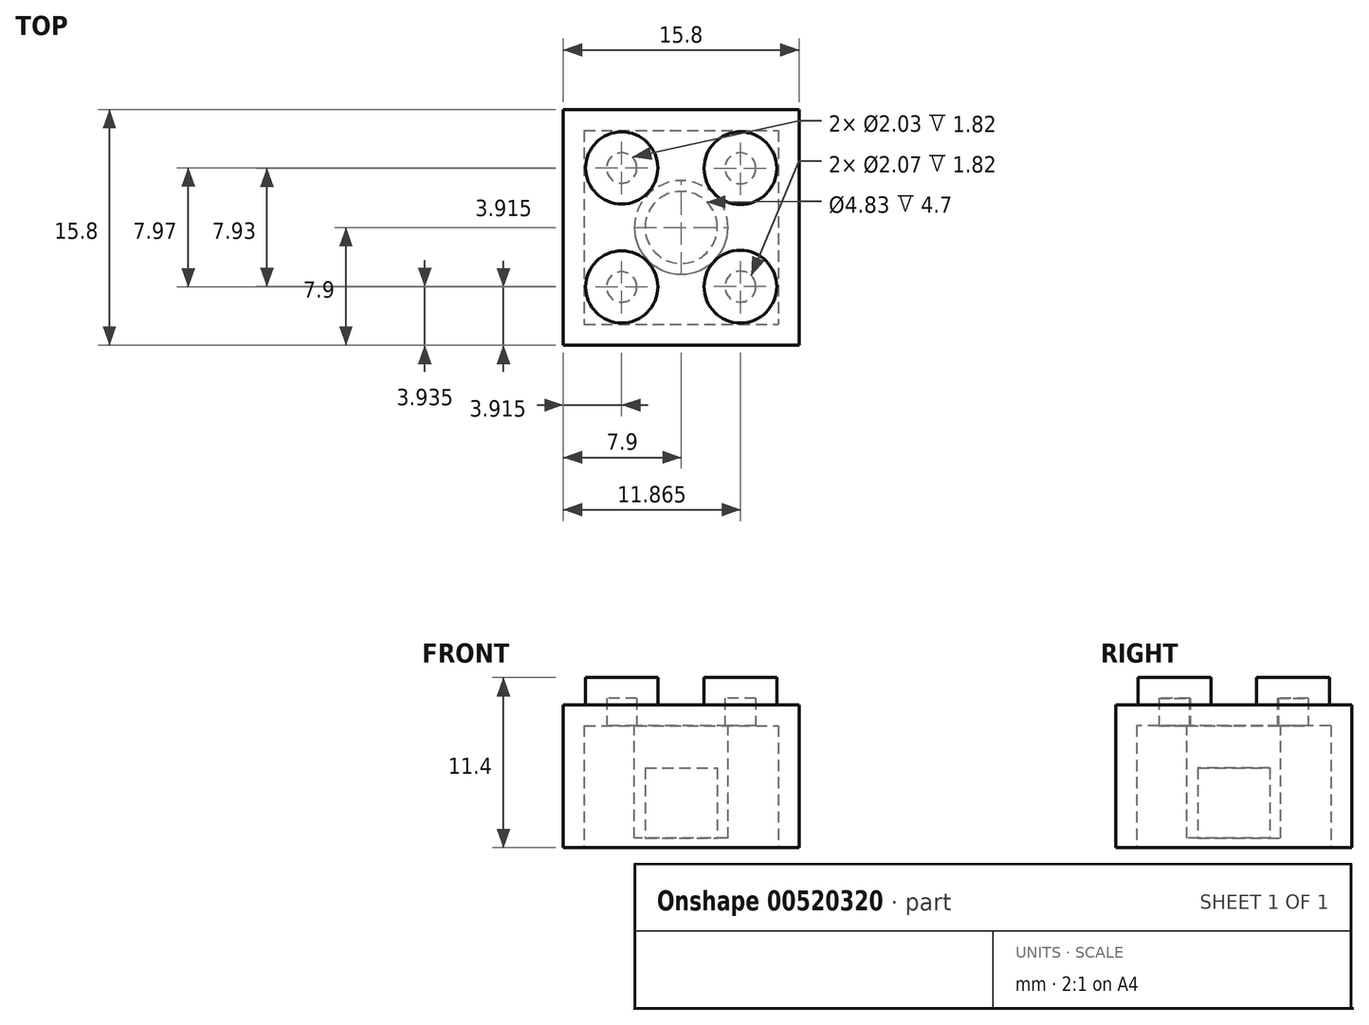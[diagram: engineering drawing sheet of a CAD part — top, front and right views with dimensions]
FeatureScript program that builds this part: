
annotation { "Feature Type Name" : "Feature", "Feature Type Description" : "" }
export const myFeature = defineFeature(function(context is Context, id is Id, definition is map)
    precondition{}
    {
        {
            var Q0;
            Q0=qCreatedBy(makeId("Top.planeOp"),FACE);
            var sketch = newSketch(context, id + "F0", { "sketchPlane" : qUnion([Q0])});
            skPoint(sketch, "E0.middle", {"position": v(0, 0) * mm});
            skCircle(sketch, "E1.MirrorC", {"center": v(-3.98, 3.98) * mm, "radius": 2.42 * mm});
            skCircle(sketch, "E2.MirrorC", {"center": v(3.97, 3.96) * mm, "radius": 2.44 * mm});
            skCircle(sketch, "E3.MirrorC", {"center": v(3.97, -3.97) * mm, "radius": 2.44 * mm});
            skCircle(sketch, "E4.MirrorC", {"center": v(-3.98, -3.98) * mm, "radius": 2.42 * mm});
            skPoint(sketch, "E0.left.start.orphan", {"position": v(-7.9, 7.9) * mm});
            skPoint(sketch, "E0.right.start.orphan", {"position": v(7.9, 7.9) * mm});
            skPoint(sketch, "E0.top.end.orphan", {"position": v(7.9, -7.9) * mm});
            skPoint(sketch, "E0.top.start.orphan", {"position": v(-7.9, -7.9) * mm});
            skSolve(sketch);
        }
        {
            var Q0;
            Q0=qCreatedBy(makeId("Top.planeOp"),FACE);
            var sketch = newSketch(context, id + "F1", { "sketchPlane" : qUnion([Q0])});
            skLineSegment(sketch, "E5.bottom", {"start": v(-7.9, 7.9) * mm, "end": v(7.9, 7.9) * mm});
            skLineSegment(sketch, "E5.top", {"start": v(-7.9, -7.9) * mm, "end": v(7.9, -7.9) * mm});
            skLineSegment(sketch, "E5.left", {"start": v(-7.9, 7.9) * mm, "end": v(-7.9, -7.9) * mm});
            skLineSegment(sketch, "E5.right", {"start": v(7.9, 7.9) * mm, "end": v(7.9, -7.9) * mm});
            skPoint(sketch, "E5.middle", {"position": v(0, 0) * mm});
            skSolve(sketch);
        }
        {
            var Q0;
            Q0 = qSketchRegion(id + "F1", true);
            extrude(context, id + "F2", {"entities" : qUnion([Q0]), "depth" : 9.58 * mm, "offsetDistance" : 25 * mm});
        }
        {
            var Q0;
            Q0 = qSketchRegion(id + "F0", true);
            extrude(context, id + "F3", {"entities" : qUnion([Q0]), "operationType" : NewBodyOperationType.ADD, "depth" : 11.4 * mm, "offsetDistance" : 25 * mm});
        }
        {
            var Q0;
            Q0=makeQuery(id+"F2.opExtrude","CAP_FACE",FACE,{"disambiguationData":[OSD([sQuery(id+"F1.wireOp",EDGE,"E5.bottom"),sQuery(id+"F1.wireOp",EDGE,"E5.top"),sQuery(id+"F1.wireOp",EDGE,"E5.left"),sQuery(id+"F1.wireOp",EDGE,"E5.right")])],"isStart":true});
            shell(context, id + "F4", {"entities" : qUnion([Q0]), "thickness" : 1.4 * mm});
        }
        {
            var Q0;
            Q0=makeQuery(id+"F4.opShell","OFFSET_FACE",FACE,{"disambiguationData":[OSD([sQuery(id+"F1.wireOp",EDGE,"E5.bottom"),sQuery(id+"F1.wireOp",EDGE,"E5.top"),sQuery(id+"F1.wireOp",EDGE,"E5.left"),sQuery(id+"F1.wireOp",EDGE,"E5.right")])]});
            var sketch = newSketch(context, id + "F5", { "sketchPlane" : qUnion([Q0])});
            skCircle(sketch, "E6", {"center": v(0, 0) * mm, "radius": 3.13 * mm});
            skSolve(sketch);
        }
        {
            var Q0;
            Q0 = qSketchRegion(id + "F5", true);
            extrude(context, id + "F6", {"entities" : qUnion([Q0]), "operationType" : NewBodyOperationType.ADD, "depth" : 7.54 * mm, "offsetDistance" : 25 * mm});
        }
        {
            var Q0;
            Q0=makeQuery(id+"F6.opExtrude","CAP_FACE",FACE,{"disambiguationData":[OSD([sQuery(id+"F5.wireOp",EDGE,"E6")])],"isStart":false});
            var sketch = newSketch(context, id + "F7", { "sketchPlane" : qUnion([Q0])});
            skCircle(sketch, "E7", {"center": v(0, 0) * mm, "radius": 2.42 * mm});
            skSolve(sketch);
        }
        {
            var Q0;
            Q0 = qSketchRegion(id + "F7", true);
            extrude(context, id + "F8", {"entities" : qUnion([Q0]), "operationType" : NewBodyOperationType.REMOVE, "oppositeDirection" : true, "depth" : 4.7 * mm, "offsetDistance" : 25 * mm});
        }
    });
